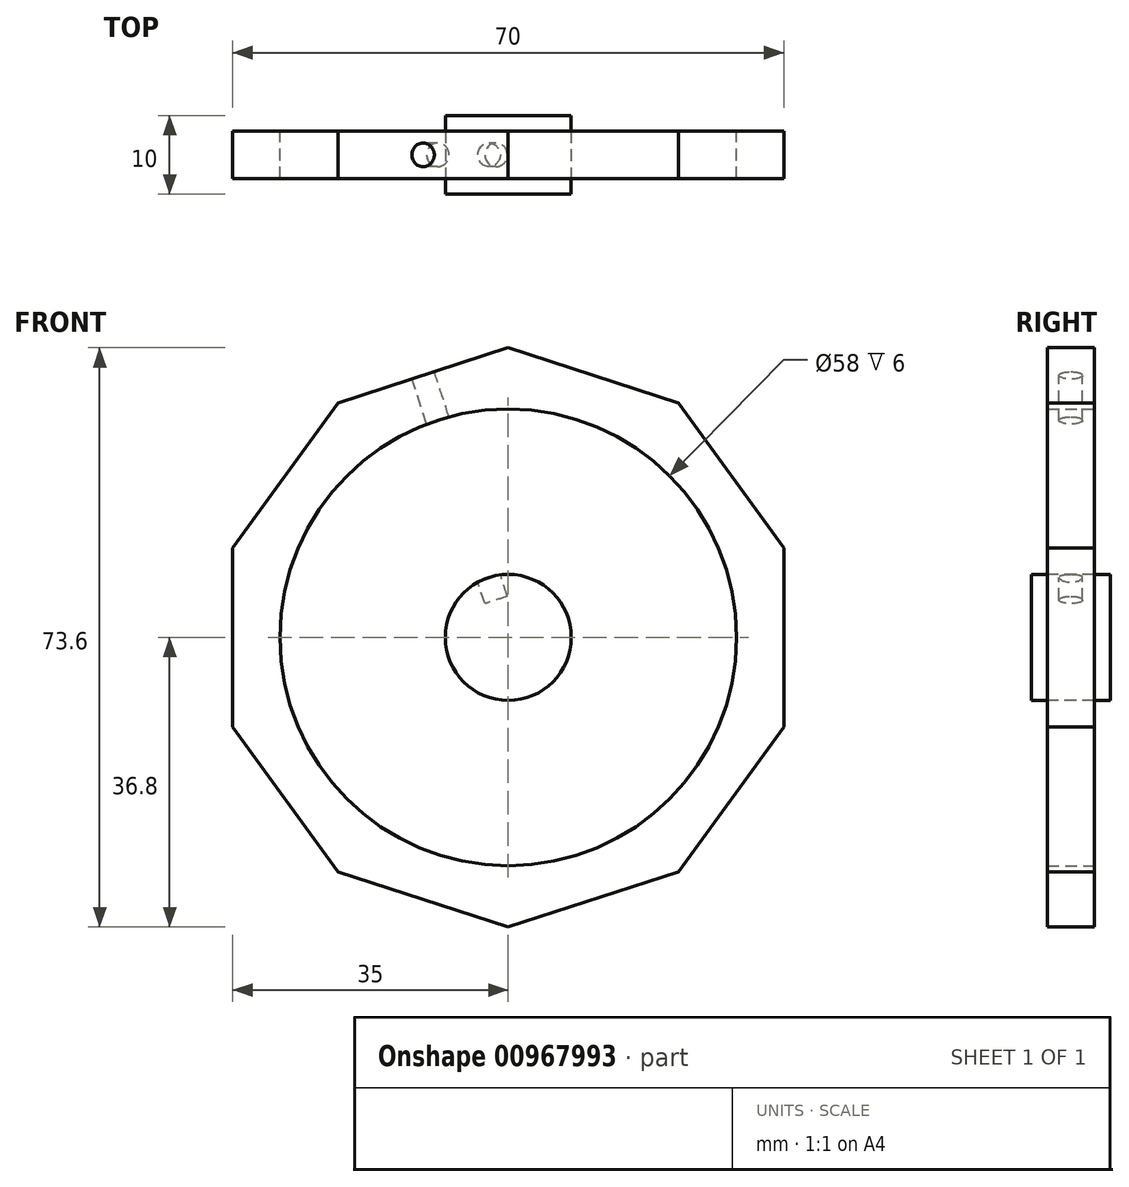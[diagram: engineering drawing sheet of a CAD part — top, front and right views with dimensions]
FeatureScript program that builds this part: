
annotation { "Feature Type Name" : "Feature", "Feature Type Description" : "" }
export const myFeature = defineFeature(function(context is Context, id is Id, definition is map)
    precondition{}
    {
        {
            var Q0;
            Q0=qCreatedBy(makeId("Front.planeOp"),FACE);
            var sketch = newSketch(context, id + "F0", { "sketchPlane" : qUnion([Q0])});
            skCircle(sketch, "E0.cCircle", {"center": v(0, 0) * mm, "radius": 35 * mm, "construction": true});
            skLineSegment(sketch, "E0.0", {"start": v(35, -11.37) * mm, "end": v(21.63, -29.77) * mm});
            skLineSegment(sketch, "E0.1", {"start": v(21.63, -29.77) * mm, "end": v(0, -36.8) * mm});
            skLineSegment(sketch, "E0.2", {"start": v(0, -36.8) * mm, "end": v(-21.63, -29.77) * mm});
            skLineSegment(sketch, "E0.3", {"start": v(-21.63, -29.77) * mm, "end": v(-35, -11.37) * mm});
            skLineSegment(sketch, "E0.4", {"start": v(-35, -11.37) * mm, "end": v(-35, 11.37) * mm});
            skLineSegment(sketch, "E0.5", {"start": v(-35, 11.37) * mm, "end": v(-21.63, 29.77) * mm});
            skLineSegment(sketch, "E0.6", {"start": v(-21.63, 29.77) * mm, "end": v(0, 36.8) * mm});
            skLineSegment(sketch, "E0.7", {"start": v(0, 36.8) * mm, "end": v(21.63, 29.77) * mm});
            skLineSegment(sketch, "E0.8", {"start": v(21.63, 29.77) * mm, "end": v(35, 11.37) * mm});
            skLineSegment(sketch, "E0.9", {"start": v(35, 11.37) * mm, "end": v(35, -11.37) * mm});
            skPoint(sketch, "E0.0.midPoint", {"position": v(28.32, -20.57) * mm});
            skSolve(sketch);
        }
        {
            var Q0;
            Q0=makeQuery(id+"F0.imprint","IMPRINT",FACE,{"disambiguationData":[TD([[makeQuery(id+"F0.imprint","IMPRINT",EDGE,{"derivedFrom":sQuery(id+"F0.wireOp",EDGE,"E0.0")}),-1.0]])]});
            extrude(context, id + "F1", {"entities" : qUnion([Q0]), "depth" : 6 * mm, "offsetDistance" : 25 * mm, "symmetric" : true});
        }
        {
            var Q0;
            Q0=makeQuery(id+"F1.opExtrude","SWEPT_FACE",FACE,{"disambiguationData":[OSD([sQuery(id+"F0.wireOp",EDGE,"E0.6")])]});
            var sketch = newSketch(context, id + "F2", { "sketchPlane" : qUnion([Q0])});
            skCircle(sketch, "E1", {"center": v(0, 0) * mm, "radius": 1.5 * mm});
            skSolve(sketch);
        }
        {
            var Q0;
            Q0=makeQuery(id+"F1.opExtrude","CAP_FACE",FACE,{"disambiguationData":[OSD([sQuery(id+"F0.wireOp",EDGE,"E0.0"),sQuery(id+"F0.wireOp",EDGE,"E0.1"),sQuery(id+"F0.wireOp",EDGE,"E0.2"),sQuery(id+"F0.wireOp",EDGE,"E0.3"),sQuery(id+"F0.wireOp",EDGE,"E0.4"),sQuery(id+"F0.wireOp",EDGE,"E0.5"),sQuery(id+"F0.wireOp",EDGE,"E0.6"),sQuery(id+"F0.wireOp",EDGE,"E0.7"),sQuery(id+"F0.wireOp",EDGE,"E0.8"),sQuery(id+"F0.wireOp",EDGE,"E0.9")])],"isStart":true});
            var sketch = newSketch(context, id + "F3", { "sketchPlane" : qUnion([Q0])});
            skCircle(sketch, "E2", {"center": v(0, 0) * mm, "radius": 29 * mm});
            skCircle(sketch, "E3", {"center": v(0, 0) * mm, "radius": 8 * mm});
            skSolve(sketch);
        }
        {
            var Q0;
            Q0=makeQuery(id+"F3.imprint","IMPRINT",FACE,{"disambiguationData":[TD([[makeQuery(id+"F3.imprint","IMPRINT",EDGE,{"derivedFrom":sQuery(id+"F3.wireOp",EDGE,"E2")}),1.0]])]});
            var sketch = newSketch(context, id + "F4", { "sketchPlane" : qUnion([Q0])});
            skCircle(sketch, "E4", {"center": v(0, 0) * mm, "radius": 8 * mm});
            skSolve(sketch);
        }
        {
            var Q0;
            Q0=qSketchRegion(id+"F4",true);
            extrude(context, id + "F5", {"entities" : qUnion([Q0]), "operationType" : NewBodyOperationType.ADD, "depth" : 2 * mm, "offsetDistance" : 25 * mm, "hasSecondDirection" : true, "secondDirectionOppositeDirection" : true, "secondDirectionDepth" : 8 * mm});
        }
        {
            var Q0;
            Q0=makeQuery(id+"F3.imprint","IMPRINT",FACE,{"disambiguationData":[TD([[makeQuery(id+"F3.imprint","IMPRINT",EDGE,{"derivedFrom":sQuery(id+"F3.wireOp",EDGE,"E2")}),1.0]])]});
            extrude(context, id + "F6", {"entities" : qUnion([Q0]), "operationType" : NewBodyOperationType.REMOVE, "oppositeDirection" : true, "depth" : 6 * mm, "offsetDistance" : 25 * mm});
        }
        {
            var Q0;
            Q0=makeQuery(id+"F2.imprint","IMPRINT",FACE,{"disambiguationData":[TD([[makeQuery(id+"F2.imprint","IMPRINT",EDGE,{"derivedFrom":sQuery(id+"F2.wireOp",EDGE,"E1")}),1.0]])]});
            extrude(context, id + "F7", {"entities" : qUnion([Q0]), "operationType" : NewBodyOperationType.REMOVE, "oppositeDirection" : true, "depth" : 30 * mm, "offsetDistance" : 25 * mm});
        }
    });
